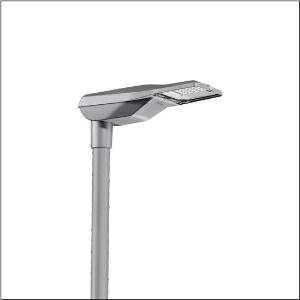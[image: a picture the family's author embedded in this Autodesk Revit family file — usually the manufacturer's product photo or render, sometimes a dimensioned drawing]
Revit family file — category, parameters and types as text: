
# Revit family: streetlight_sl_21_iq_micro___st0_8a_5xe1c31g08cb_6ed2
name_source: partatom
category: Lighting Fixtures
units: mm (PartAtom-declared; Revit-internal decimal feet)

## family parameters
Cut with Voids When Loaded = No
Host = Face
Light Source = No
Part Type = Normal
Room Calculation Point = No
Round Connector Dimension = Use Diameter
Shared = No

## types (1)
- --- (1 x LED, 2870 lm, 19.4 W, 3000K)
    Apparent Load = 19 VA
    CIE Flux Codes = 38 75 97 100 100
    Color Rendering = 70
    Color Temperature = 3000K
    Default Elevation = 1800 mm
    Description = Streetlight SL 21 iQ micro, mast luminaire, primary light control with lens, of PMMA, primary optical cover: cover, of toughened safety glass, transparent, light distribution: ST0.8a, light emission: direct distribution, primary light characteristic: asymmetric, installation type: post-top, side-entry, LED, High Power LED, rated luminous flux: 2.870lm, luminous efficacy: 148lm/W, light colour: 730, colour temperature: 3000K, control gear: iQ Street-Remote, control: Street-Remote, Auto-Match, Temp-Guard, Lumen-Switch, Night-Set, Smart-Wire, Light-Fading, Desk-Remote (wireless, voltage-free reading and setting of iQ features in the workshop via application-optimized NFC function/RFID function), optimised constant luminous flux control (CLO 2.0), pre-setting: linear dimming characteristic, mains connection: 220..240V, AC, 50/60Hz, start of lifetime: 19W, end of service life: 20W, reduction: 10W, luminaire housing, of diecast aluminium, powder-coated, Siteco® metallic grey (DB 702S), corrosivity category C5 high according to DIN EN ISO 12944, please order mast flange separately, inclination adjustable: 0°, 5°, 10°, 15°, sealing non-destructively replaceable, multi-level sealing system, length: 528mm, width: 235mm, height: 110mm, mast flange for spigot size: 42mm (side-entry): 5XC10008XM4, 60/48mm (side-entry/post-top): 5XC10108XM2, 76/60mm (side-entry/post-top): 5XC10108XM1, protection rating (complete): IP66, insulation class (complete): insulation class II (safety insulation), certification: CE, ENEC, ENEC+, VDE, impact resistance: IK10, permissible operating ambient temperature for outdoor applications: -40..+50°C, standard-compliant lighting for roads and squares, packaging unit: 1 piece

Light Distribution: ST0.8a
    Height = 110 mm
    Lamp = 1 x LED
    Lamp Light Flux = 2870 lm
    Lamp Power = 19.4 W
    Lamp count = 1
    Length = 528 mm
    Luminous efficacy = 148 lm/W
    Manufacturer = Siteco
    ModVariant = No
    Model = 5XE1C31G08CB
    Number of Poles = 1
    OnlyDefault = Yes
    Power Factor = 1
    Product Name = Streetlight SL 21 iQ micro | ST0.8a
    Product group = mast luminaire | pylon top
    ProductGroupID = 6100
    Protection Class = Protection class II
    Protection Degree = IP 66
    RLX_Detail_Level = 1
    RLX_Emergency_Light_Flux = 0 lm
    RLX_Emergency_Type = 0
    RLX_Emergency_Type_DB = No
    RlxData = <blob elided: 99057 chars, md5=9f60a0ab>
    Socket = socket
    Standby Power = 0 W
    System Light Flux = 2870 lm
    System Power = 19 W
    Type Comments = factory setting: luminous flux: 100 % | dim-lin: 254 | 387 mA
    Type Image = l_1006881.jpg
    URL = http://relux.com
    VarID = @adj_141705
    Voltage = 0 V
    Weight = 0.00 kg
    Width = 235 mm

## geometry (parser evidence)
native form markers: Blend x4, Sweep x10
no freeform markers — native parametric forms only
